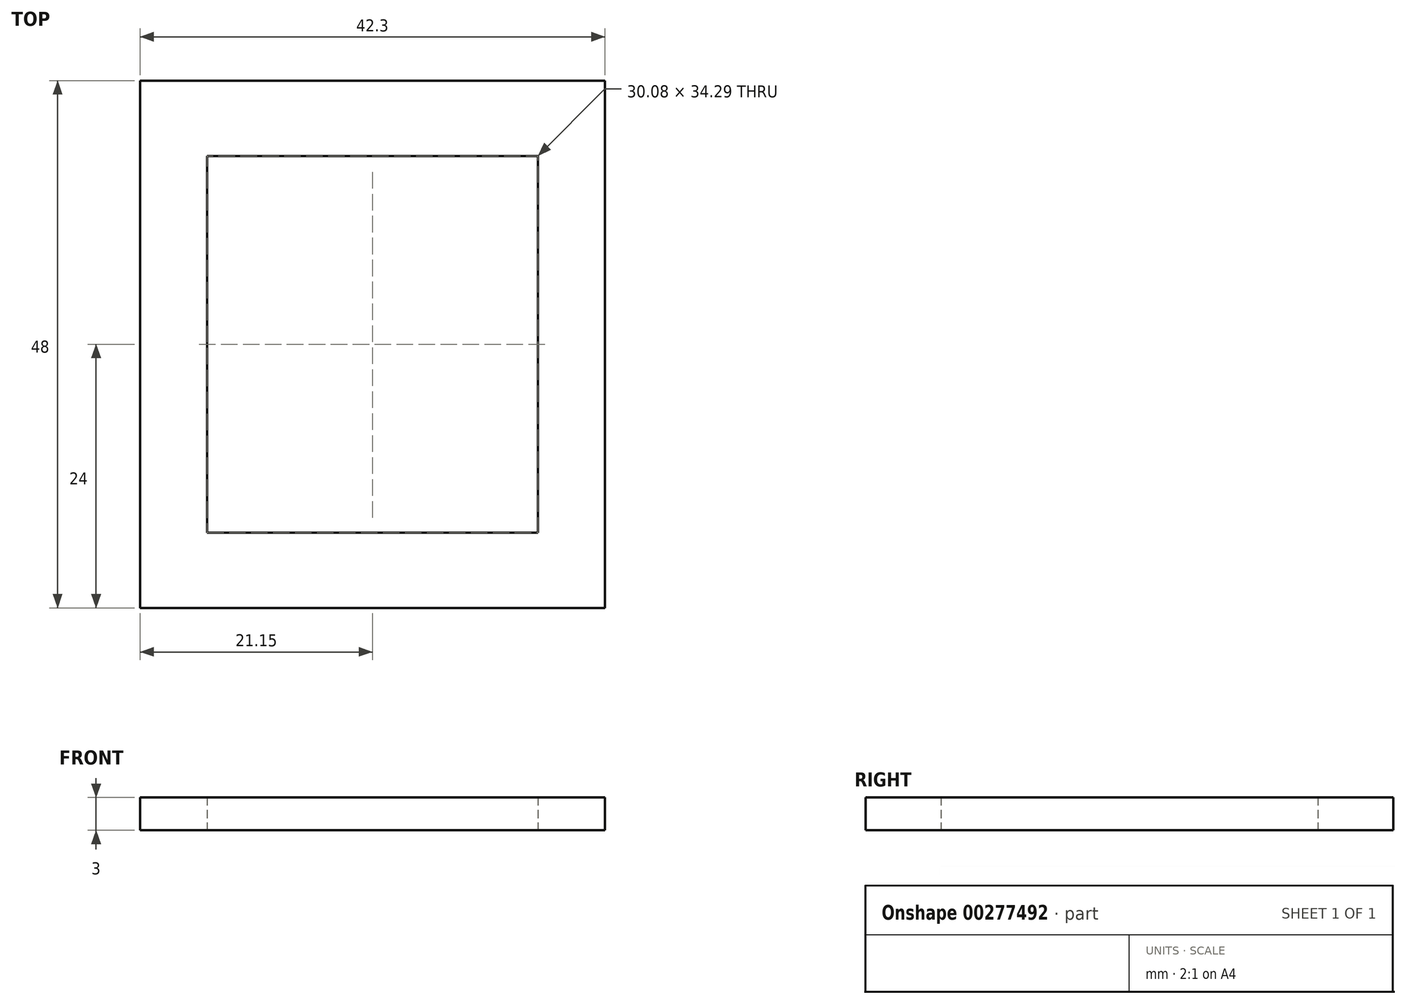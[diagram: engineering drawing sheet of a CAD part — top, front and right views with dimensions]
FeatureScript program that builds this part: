
annotation { "Feature Type Name" : "Feature", "Feature Type Description" : "" }
export const myFeature = defineFeature(function(context is Context, id is Id, definition is map)
    precondition{}
    {
        {
            var Q0;
            Q0=qCreatedBy(makeId("Top.planeOp"),FACE);
            var sketch = newSketch(context, id + "F0", { "sketchPlane" : qUnion([Q0])});
            skLineSegment(sketch, "E0.bottom", {"start": v(21.15, 24) * mm, "end": v(-21.15, 24) * mm});
            skLineSegment(sketch, "E0.top", {"start": v(21.15, -24) * mm, "end": v(-21.15, -24) * mm});
            skLineSegment(sketch, "E0.left", {"start": v(21.15, 24) * mm, "end": v(21.15, -24) * mm});
            skLineSegment(sketch, "E0.right", {"start": v(-21.15, 24) * mm, "end": v(-21.15, -24) * mm});
            skPoint(sketch, "E0.middle", {"position": v(0, 0) * mm});
            skLineSegment(sketch, "E1.bottom", {"start": v(15.04, 17.15) * mm, "end": v(-15.04, 17.15) * mm});
            skLineSegment(sketch, "E1.top", {"start": v(15.04, -17.15) * mm, "end": v(-15.04, -17.15) * mm});
            skLineSegment(sketch, "E1.left", {"start": v(15.04, 17.15) * mm, "end": v(15.04, -17.15) * mm});
            skLineSegment(sketch, "E1.right", {"start": v(-15.04, 17.15) * mm, "end": v(-15.04, -17.15) * mm});
            skSolve(sketch);
        }
        {
            var Q0;
            Q0=makeQuery(id+"F0.imprint","IMPRINT",FACE,{"disambiguationData":[TD([[makeQuery(id+"F0.imprint","IMPRINT",EDGE,{"derivedFrom":sQuery(id+"F0.wireOp",EDGE,"E0.bottom")}),1.0]])]});
            extrude(context, id + "F1", {"entities" : qUnion([Q0]), "depth" : 3 * mm});
        }
    });
